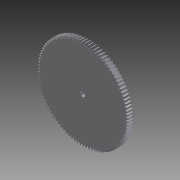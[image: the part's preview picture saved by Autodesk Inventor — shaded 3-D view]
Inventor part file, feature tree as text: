
AUTODESK INVENTOR PART (.ipt)
format: ipt  version: 2013 SP2 (Build 170200200, 200)  size: 844,288 bytes
history: native  units: in
note: dims shown in document units (in); Inventor stores cm internally (conversion verified against a paired STEP export)
features: extrude x3, sketch x3, imported_body x1
ambient origin geometry x8: Origin, YZ Plane, XZ Plane, XY Plane, X Axis, Y Axis, Z Axis, Center Point
bodies: Solid1 (feature_tree)
feature tree (7):
  imported_body  "Base1"
  extrude  "Extrusion2"  Depth=0.66in TaperAngle=0.0deg
  extrude  "Extrusion3"  Depth=0.41in TaperAngle=0.0deg
  extrude  "Extrusion4"  Depth=0.171in
  sketch  "Sketch2"  dims[d6=0.215in d7=0.66in d8=0.0in]
  sketch  "Sketch3"  dims[d9=0.7in d11=0.41in d12=0.0in]
  sketch  "Sketch4"  dims[d13=0.15in d14=0.171in d15=0.3in d16=0.0in]
